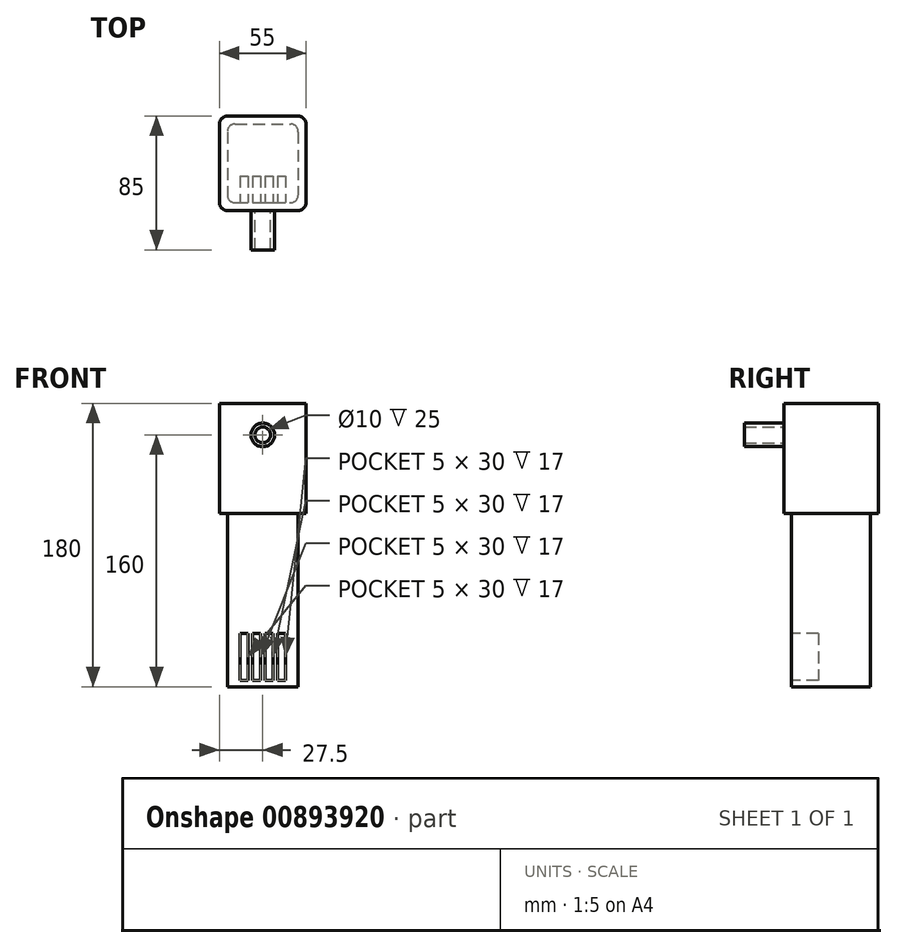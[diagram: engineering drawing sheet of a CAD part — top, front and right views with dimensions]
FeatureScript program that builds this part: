
annotation { "Feature Type Name" : "Feature", "Feature Type Description" : "" }
export const myFeature = defineFeature(function(context is Context, id is Id, definition is map)
    precondition{}
    {
        {
            var Q0;
            Q0=qCreatedBy(makeId("Top.planeOp"),FACE);
            var sketch = newSketch(context, id + "F0", { "sketchPlane" : qUnion([Q0])});
            skLineSegment(sketch, "E0.bottom", {"start": v(-22.5, 25) * mm, "end": v(22.5, 25) * mm});
            skLineSegment(sketch, "E0.top", {"start": v(-22.5, -25) * mm, "end": v(22.5, -25) * mm});
            skLineSegment(sketch, "E0.left", {"start": v(-22.5, 25) * mm, "end": v(-22.5, -25) * mm});
            skLineSegment(sketch, "E0.right", {"start": v(22.5, 25) * mm, "end": v(22.5, -25) * mm});
            skLineSegment(sketch, "E1", {"start": v(0, 25) * mm, "end": v(0, -25) * mm, "construction": true});
            skPoint(sketch, "E2", {"position": v(0, 0) * mm});
            skSolve(sketch);
        }
        {
            var Q0;
            Q0=makeQuery(id+"F0.imprint","IMPRINT",FACE,{"disambiguationData":[TD([[makeQuery(id+"F0.imprint","IMPRINT",EDGE,{"derivedFrom":sQuery(id+"F0.wireOp",EDGE,"E0.bottom")}),-1.0]])]});
            extrude(context, id + "F1", {"entities" : qUnion([Q0]), "depth" : 110 * mm, "offsetDistance" : 25 * mm});
        }
        {
            var Q0;
            Q0=makeQuery(id+"F1.opExtrude","CAP_FACE",FACE,{"disambiguationData":[OSD([sQuery(id+"F0.wireOp",EDGE,"E0.bottom"),sQuery(id+"F0.wireOp",EDGE,"E0.top"),sQuery(id+"F0.wireOp",EDGE,"E0.left"),sQuery(id+"F0.wireOp",EDGE,"E0.right")])],"isStart":false});
            var sketch = newSketch(context, id + "F2", { "sketchPlane" : qUnion([Q0])});
            skPoint(sketch, "E3", {"position": v(0, 0) * mm});
            skLineSegment(sketch, "E4.bottom", {"start": v(-22.5, -30) * mm, "end": v(22.5, -30) * mm});
            skLineSegment(sketch, "E4.top", {"start": v(-22.5, 30) * mm, "end": v(22.5, 30) * mm});
            skLineSegment(sketch, "E4.left", {"start": v(-27.5, -25) * mm, "end": v(-27.5, 25) * mm});
            skLineSegment(sketch, "E4.right", {"start": v(27.5, -25) * mm, "end": v(27.5, 25) * mm});
            skLineSegment(sketch, "E5", {"start": v(0, 30) * mm, "end": v(0, -30) * mm, "construction": true});
            skPoint(sketch, "E6.visualSharp", {"position": v(27.5, 30) * mm});
            skArc(sketch, "E6.filletArc", {"start": v(27.5, 25) * mm, "mid": v(26.04, 28.54) * mm, "end": v(22.5, 30) * mm});
            skPoint(sketch, "E7.visualSharp", {"position": v(27.5, -30) * mm});
            skArc(sketch, "E7.filletArc", {"start": v(22.5, -30) * mm, "mid": v(26.04, -28.54) * mm, "end": v(27.5, -25) * mm});
            skPoint(sketch, "E8.visualSharp", {"position": v(-27.5, -30) * mm});
            skArc(sketch, "E8.filletArc", {"start": v(-27.5, -25) * mm, "mid": v(-26.04, -28.54) * mm, "end": v(-22.5, -30) * mm});
            skPoint(sketch, "E9.visualSharp", {"position": v(-27.5, 30) * mm});
            skArc(sketch, "E9.filletArc", {"start": v(-22.5, 30) * mm, "mid": v(-26.04, 28.54) * mm, "end": v(-27.5, 25) * mm});
            skSolve(sketch);
        }
        {
            var Q0;
            Q0=makeQuery(id+"F2.imprint","IMPRINT",FACE,{"disambiguationData":[TD([[makeQuery(id+"F2.imprint","IMPRINT",EDGE,{"derivedFrom":makeQuery(id+"F1.opExtrude","CAP_EDGE",EDGE,{"disambiguationData":[OSD([sQuery(id+"F0.wireOp",EDGE,"E0.bottom")])],"isStart":false})}),-1.0]])]});
            var Q1;
            Q1=makeQuery(id+"F2.imprint","IMPRINT",FACE,{"disambiguationData":[TD([[makeQuery(id+"F2.imprint","IMPRINT",EDGE,{"derivedFrom":sQuery(id+"F2.wireOp",EDGE,"E4.bottom")}),1.0]])]});
            extrude(context, id + "F3", {"entities" : qUnion([Q0, Q1]), "operationType" : NewBodyOperationType.ADD, "depth" : 70 * mm, "offsetDistance" : 25 * mm});
        }
        {
            var Q0;
            Q0=makeQuery(id+"F1.opExtrude","SWEPT_EDGE",EDGE,{"disambiguationData":[OSD([sQuery(id+"F0.wireOp",EDGE,"E0.bottom"),sQuery(id+"F0.wireOp",EDGE,"E0.right")])]});
            var Q1;
            Q1=makeQuery(id+"F1.opExtrude","SWEPT_EDGE",EDGE,{"disambiguationData":[OSD([sQuery(id+"F0.wireOp",EDGE,"E0.top"),sQuery(id+"F0.wireOp",EDGE,"E0.right")])]});
            var Q2;
            Q2=makeQuery(id+"F1.opExtrude","SWEPT_EDGE",EDGE,{"disambiguationData":[OSD([sQuery(id+"F0.wireOp",EDGE,"E0.top"),sQuery(id+"F0.wireOp",EDGE,"E0.left")])]});
            var Q3;
            Q3=makeQuery(id+"F1.opExtrude","SWEPT_EDGE",EDGE,{"disambiguationData":[OSD([sQuery(id+"F0.wireOp",EDGE,"E0.bottom"),sQuery(id+"F0.wireOp",EDGE,"E0.left")])]});
            fillet(context, id + "F4", {"entities" : qUnion([Q0, Q1, Q2, Q3]), "radius" : 5 * mm, "tangentPropagation" : true, "allowEdgeOverflow" : false});
        }
        {
            var Q0;
            Q0=makeQuery(id+"F1.opExtrude","SWEPT_FACE",FACE,{"disambiguationData":[OSD([sQuery(id+"F0.wireOp",EDGE,"E0.top")])]});
            var sketch = newSketch(context, id + "F5", { "sketchPlane" : qUnion([Q0])});
            skLineSegment(sketch, "E10.bottom", {"start": v(-14.5, 4) * mm, "end": v(-9.5, 4) * mm});
            skLineSegment(sketch, "E10.top", {"start": v(-14.5, 34) * mm, "end": v(-9.5, 34) * mm});
            skLineSegment(sketch, "E10.left", {"start": v(-14.5, 4) * mm, "end": v(-14.5, 34) * mm});
            skLineSegment(sketch, "E10.right", {"start": v(-9.5, 4) * mm, "end": v(-9.5, 34) * mm});
            skLineSegment(sketch, "E11.bottom", {"start": v(-6.5, 34) * mm, "end": v(-1.5, 34) * mm});
            skLineSegment(sketch, "E11.top", {"start": v(-6.5, 4) * mm, "end": v(-1.5, 4) * mm});
            skLineSegment(sketch, "E11.left", {"start": v(-6.5, 34) * mm, "end": v(-6.5, 4) * mm});
            skLineSegment(sketch, "E11.right", {"start": v(-1.5, 34) * mm, "end": v(-1.5, 4) * mm});
            skLineSegment(sketch, "E12.bottom", {"start": v(1.5, 34) * mm, "end": v(6.5, 34) * mm});
            skLineSegment(sketch, "E12.top", {"start": v(1.5, 4) * mm, "end": v(6.5, 4) * mm});
            skLineSegment(sketch, "E12.left", {"start": v(1.5, 34) * mm, "end": v(1.5, 4) * mm});
            skLineSegment(sketch, "E12.right", {"start": v(6.5, 34) * mm, "end": v(6.5, 4) * mm});
            skLineSegment(sketch, "E13.bottom", {"start": v(9.5, 34) * mm, "end": v(14.5, 34) * mm});
            skLineSegment(sketch, "E13.top", {"start": v(9.5, 4) * mm, "end": v(14.5, 4) * mm});
            skLineSegment(sketch, "E13.left", {"start": v(9.5, 34) * mm, "end": v(9.5, 4) * mm});
            skLineSegment(sketch, "E13.right", {"start": v(14.5, 34) * mm, "end": v(14.5, 4) * mm});
            skSolve(sketch);
        }
        {
            var Q0;
            Q0=makeQuery(id+"F5.imprint","IMPRINT",FACE,{"disambiguationData":[TD([[makeQuery(id+"F5.imprint","IMPRINT",EDGE,{"derivedFrom":sQuery(id+"F5.wireOp",EDGE,"E10.bottom")}),1.0]])]});
            var Q1;
            Q1=makeQuery(id+"F5.imprint","IMPRINT",FACE,{"disambiguationData":[TD([[makeQuery(id+"F5.imprint","IMPRINT",EDGE,{"derivedFrom":sQuery(id+"F5.wireOp",EDGE,"E11.bottom")}),-1.0]])]});
            var Q2;
            Q2=makeQuery(id+"F5.imprint","IMPRINT",FACE,{"disambiguationData":[TD([[makeQuery(id+"F5.imprint","IMPRINT",EDGE,{"derivedFrom":sQuery(id+"F5.wireOp",EDGE,"E12.bottom")}),-1.0]])]});
            var Q3;
            Q3=makeQuery(id+"F5.imprint","IMPRINT",FACE,{"disambiguationData":[TD([[makeQuery(id+"F5.imprint","IMPRINT",EDGE,{"derivedFrom":sQuery(id+"F5.wireOp",EDGE,"E13.bottom")}),-1.0]])]});
            extrude(context, id + "F6", {"entities" : qUnion([Q0, Q1, Q2, Q3]), "operationType" : NewBodyOperationType.REMOVE, "oppositeDirection" : true, "depth" : 17 * mm, "offsetDistance" : 25 * mm});
        }
        {
            var Q0;
            Q0=makeQuery(id+"F3.opExtrude","SWEPT_FACE",FACE,{"disambiguationData":[OSD([sQuery(id+"F2.wireOp",EDGE,"E4.bottom")])]});
            var sketch = newSketch(context, id + "F7", { "sketchPlane" : qUnion([Q0])});
            skCircle(sketch, "E14", {"center": v(0, 160) * mm, "radius": 7.5 * mm});
            skCircle(sketch, "E15", {"center": v(0, 160) * mm, "radius": 5 * mm});
            skSolve(sketch);
        }
        {
            var Q0;
            Q0=makeQuery(id+"F7.imprint","IMPRINT",FACE,{"disambiguationData":[TD([[makeQuery(id+"F7.imprint","IMPRINT",EDGE,{"derivedFrom":sQuery(id+"F7.wireOp",EDGE,"E14")}),1.0]])]});
            extrude(context, id + "F8", {"entities" : qUnion([Q0]), "operationType" : NewBodyOperationType.ADD, "depth" : 25 * mm, "offsetDistance" : 25 * mm});
        }
    });
